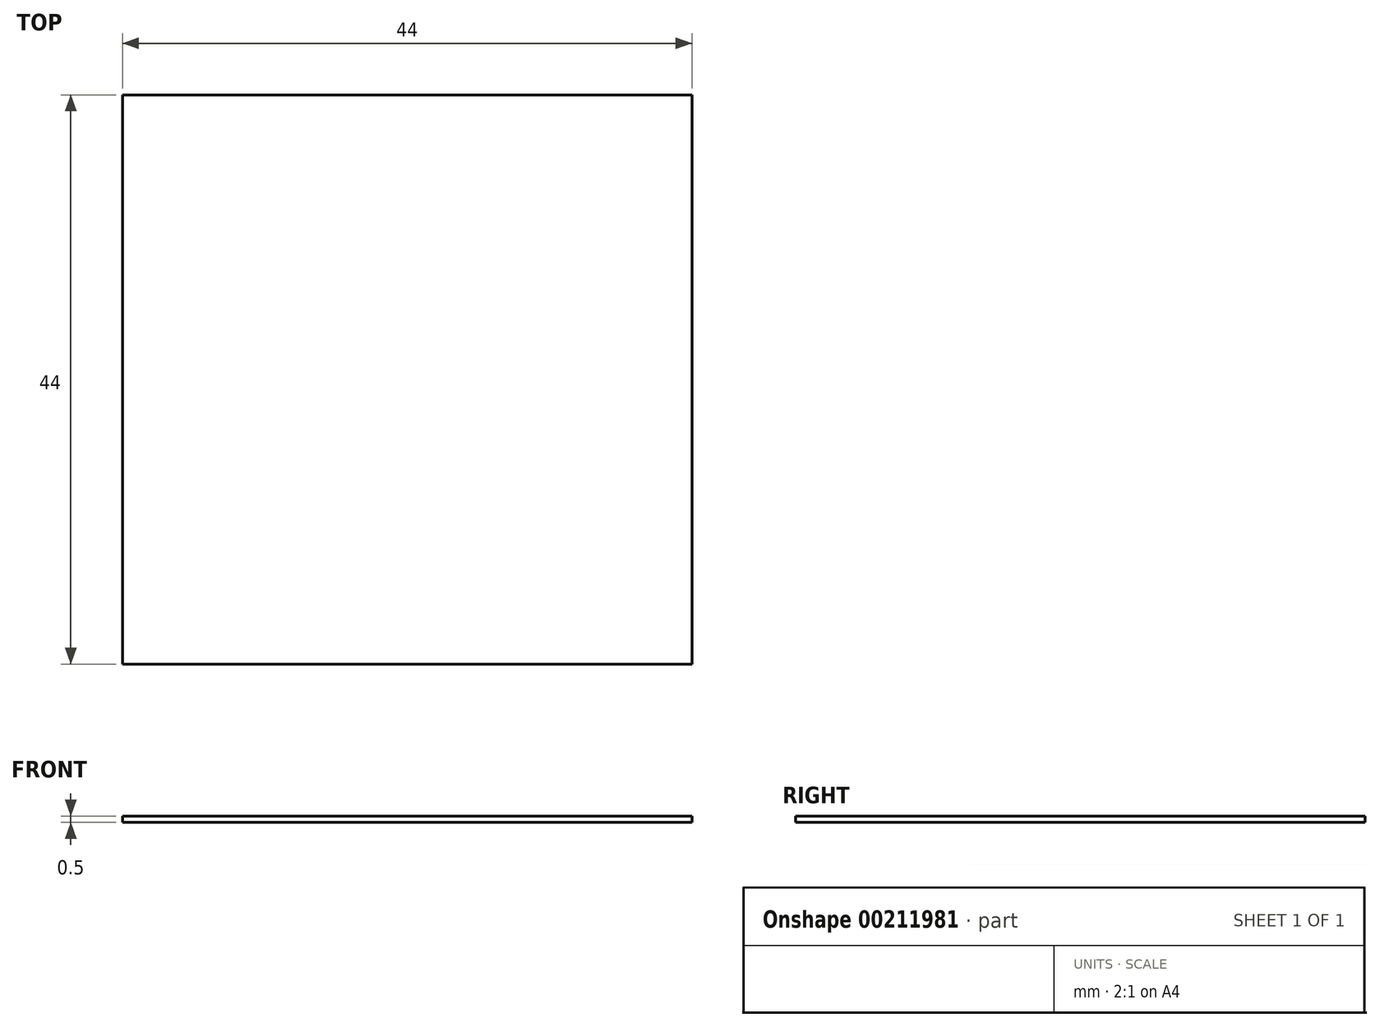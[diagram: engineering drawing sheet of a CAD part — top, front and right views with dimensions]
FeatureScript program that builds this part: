
annotation { "Feature Type Name" : "Feature", "Feature Type Description" : "" }
export const myFeature = defineFeature(function(context is Context, id is Id, definition is map)
    precondition{}
    {
        {
            var Q0;
            Q0=qCreatedBy(makeId("Top.planeOp"),FACE);
            var sketch = newSketch(context, id + "F0", { "sketchPlane" : qUnion([Q0])});
            skLineSegment(sketch, "E0.bottom", {"start": v(-22, -22) * mm, "end": v(22, -22) * mm});
            skLineSegment(sketch, "E0.top", {"start": v(-22, 22) * mm, "end": v(22, 22) * mm});
            skLineSegment(sketch, "E0.left", {"start": v(-22, -22) * mm, "end": v(-22, 22) * mm});
            skLineSegment(sketch, "E0.right", {"start": v(22, -22) * mm, "end": v(22, 22) * mm});
            skPoint(sketch, "E0.middle", {"position": v(0, 0) * mm});
            skSolve(sketch);
        }
        {
            var Q0;
            Q0 = qSketchRegion(id + "F0", true);
            extrude(context, id + "F1", {"entities" : qUnion([Q0]), "depth" : 0.5 * mm});
        }
    });
